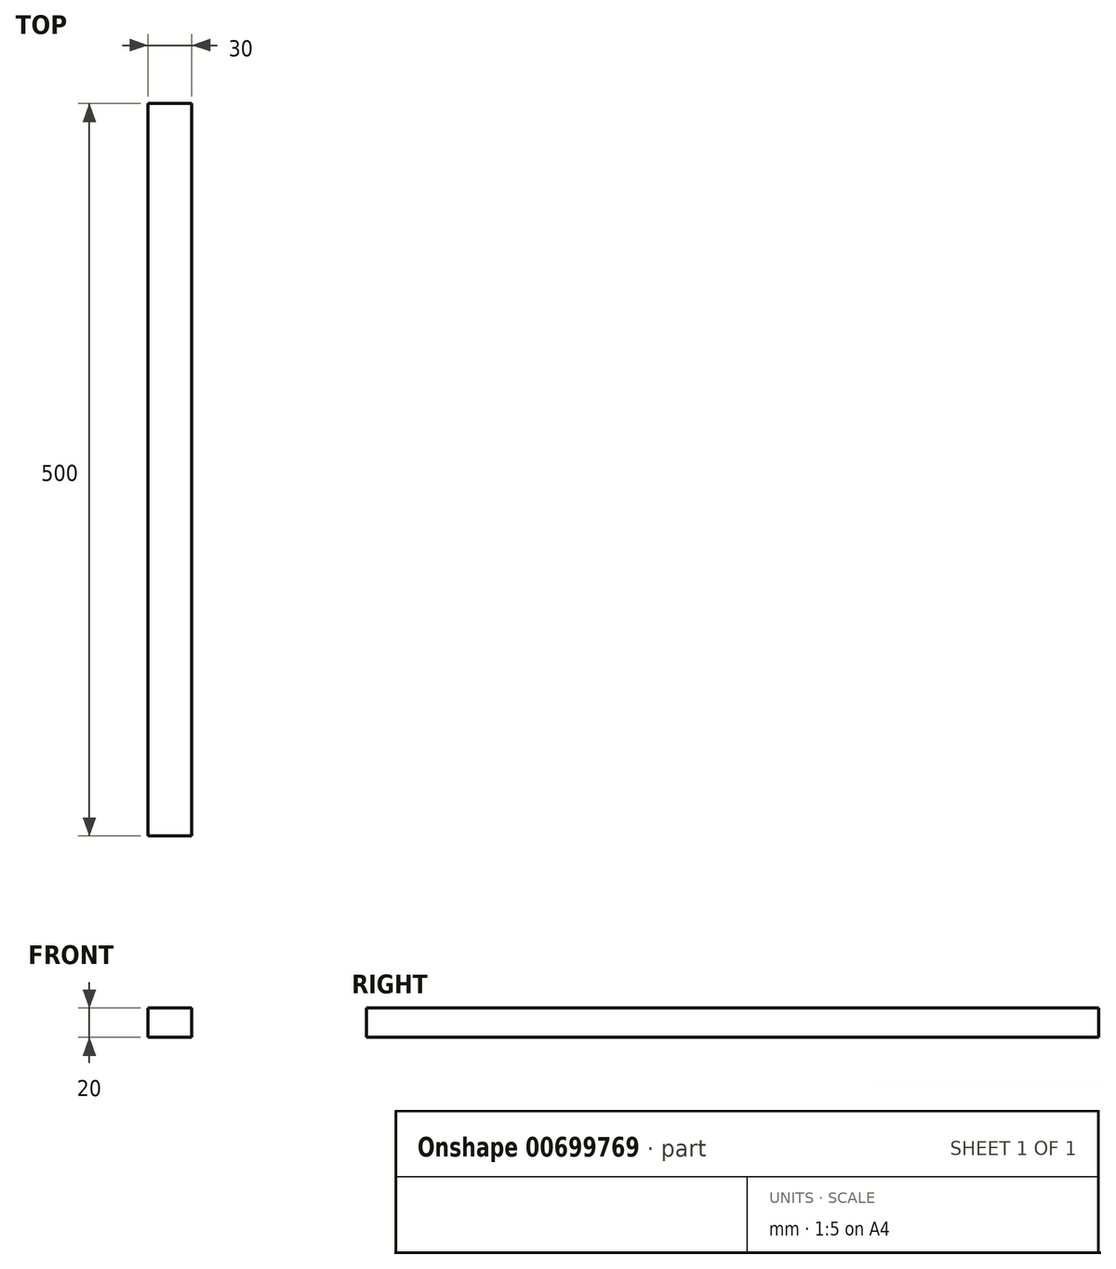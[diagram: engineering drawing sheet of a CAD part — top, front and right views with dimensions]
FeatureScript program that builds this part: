
annotation { "Feature Type Name" : "Feature", "Feature Type Description" : "" }
export const myFeature = defineFeature(function(context is Context, id is Id, definition is map)
    precondition{}
    {
        {
            var Q0;
            Q0=qCreatedBy(makeId("Top.planeOp"),FACE);
            var sketch = newSketch(context, id + "F0", { "sketchPlane" : qUnion([Q0])});
            skLineSegment(sketch, "E0.bottom", {"start": v(-15, 250) * mm, "end": v(15, 250) * mm});
            skLineSegment(sketch, "E0.top", {"start": v(-15, -250) * mm, "end": v(15, -250) * mm});
            skLineSegment(sketch, "E0.left", {"start": v(-15, 250) * mm, "end": v(-15, -250) * mm});
            skLineSegment(sketch, "E0.right", {"start": v(15, 250) * mm, "end": v(15, -250) * mm});
            skPoint(sketch, "E0.middle", {"position": v(0, 0) * mm});
            skSolve(sketch);
        }
        {
            var Q0;
            Q0=makeQuery(id+"F0.imprint","IMPRINT",FACE,{"disambiguationData":[TD([[makeQuery(id+"F0.imprint","IMPRINT",EDGE,{"derivedFrom":sQuery(id+"F0.wireOp",EDGE,"E0.bottom")}),-1.0]])]});
            extrude(context, id + "F1", {"entities" : qUnion([Q0]), "depth" : 20 * mm, "offsetDistance" : 25 * mm});
        }
        {
            var Q0;
            Q0=makeQuery(id+"F1.opExtrude","SWEPT_FACE",FACE,{"disambiguationData":[OSD([sQuery(id+"F0.wireOp",EDGE,"E0.top")])]});
            cPlane(context, id + "F2", {"entities" : qUnion([Q0]), "cplaneType" : CPlaneType.OFFSET, "offset" : 50 * mm, "oppositeDirection" : true, "width" : 150 * mm, "height" : 150 * mm});
        }
        {
            var Q0;
            Q0=makeQuery(id+"F1.opExtrude","SWEPT_FACE",FACE,{"disambiguationData":[OSD([sQuery(id+"F0.wireOp",EDGE,"E0.bottom")])]});
            cPlane(context, id + "F3", {"entities" : qUnion([Q0]), "cplaneType" : CPlaneType.OFFSET, "offset" : 50 * mm, "oppositeDirection" : true, "width" : 150 * mm, "height" : 150 * mm});
        }
    });
